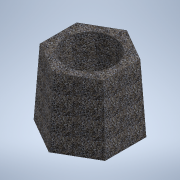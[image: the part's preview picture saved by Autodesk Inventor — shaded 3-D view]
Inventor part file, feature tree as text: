
AUTODESK INVENTOR PART (.ipt)
format: ipt  version: 2021 (Build 250183000, 183)  size: 145,920 bytes
history: native  units: mm
features: sketch x3, plane x1, loft x1, extrude x1
ambient origin geometry x8: Origin, YZ Plane, XZ Plane, XY Plane, X Axis, Y Axis, Z Axis, Center Point
bodies: Solid1 (feature_tree)
feature tree (6):
  sketch  "Sketch1"  dims[d0=750.0mm d1=700.0mm]
  plane  "Work Plane1"
  loft  "Loft1"
  extrude  "Extrusion1"  TaperAngle=0.0deg  [1 undecoded]
  sketch  "Sketch2"  dims[d2=670.0mm d3=0.0mm d4=90.0deg]
  sketch  "Sketch3"  dims[d5=0.0mm d6=90.0deg d7=510.0mm d8=620.0mm d9=0.0mm]
note: 1 required parameter value undecoded (feature->parameter linkage not recoverable at this tier; creation-order binding heuristic only, values carry confidence <= 0.55)
